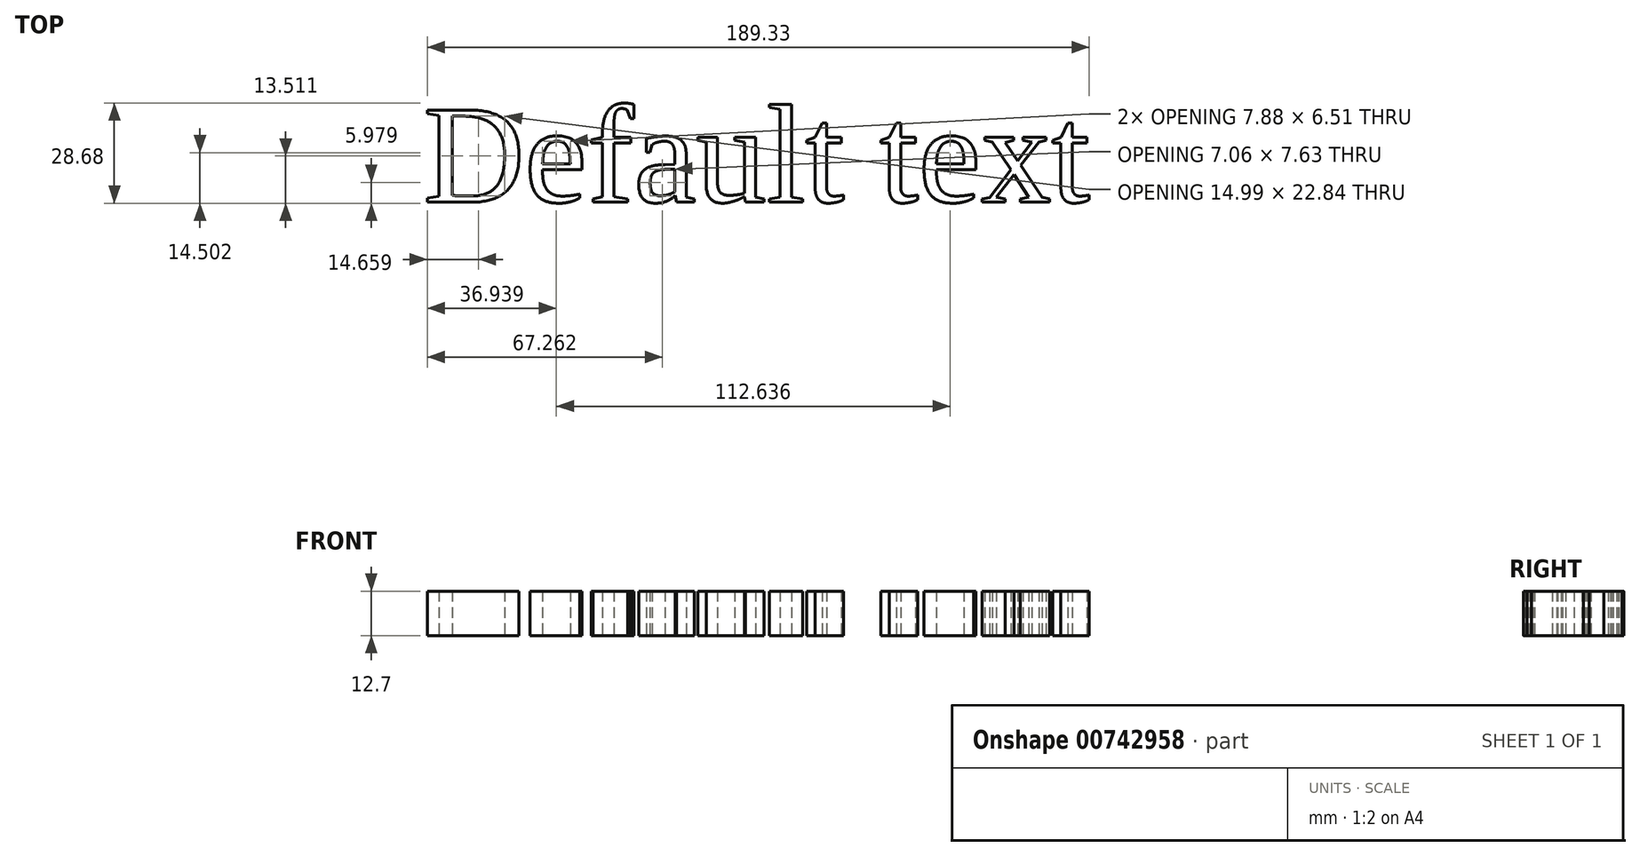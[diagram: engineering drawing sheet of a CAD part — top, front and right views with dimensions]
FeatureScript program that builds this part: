
annotation { "Feature Type Name" : "Feature", "Feature Type Description" : "" }
export const myFeature = defineFeature(function(context is Context, id is Id, definition is map)
    precondition{}
    {
        {
            var Q0;
            Q0=qCreatedBy(makeId("Top.planeOp"), FACE);
            var sketch = newSketch(context, id + "F0", { "sketchPlane" : qUnion([Q0])});
            skText(sketch, "E0", { "text": "Default text", "fontName": "Tinos-Regular.ttf"});
            const initialGuessF0  = {"E0": [-0.06574, -0.05037, 1, 0, 0.02892]};
            skSetInitialGuess(sketch, initialGuessF0);
            skSolve(sketch);
        }
        {
            var Q0;
            Q0 = qSketchRegion(id + "F0", true);
            extrude(context, id + "F1", {"entities" : qUnion([Q0]), "depth" : 12.7 * mm, "offsetDistance" : 25.4 * mm});
        }
    });
